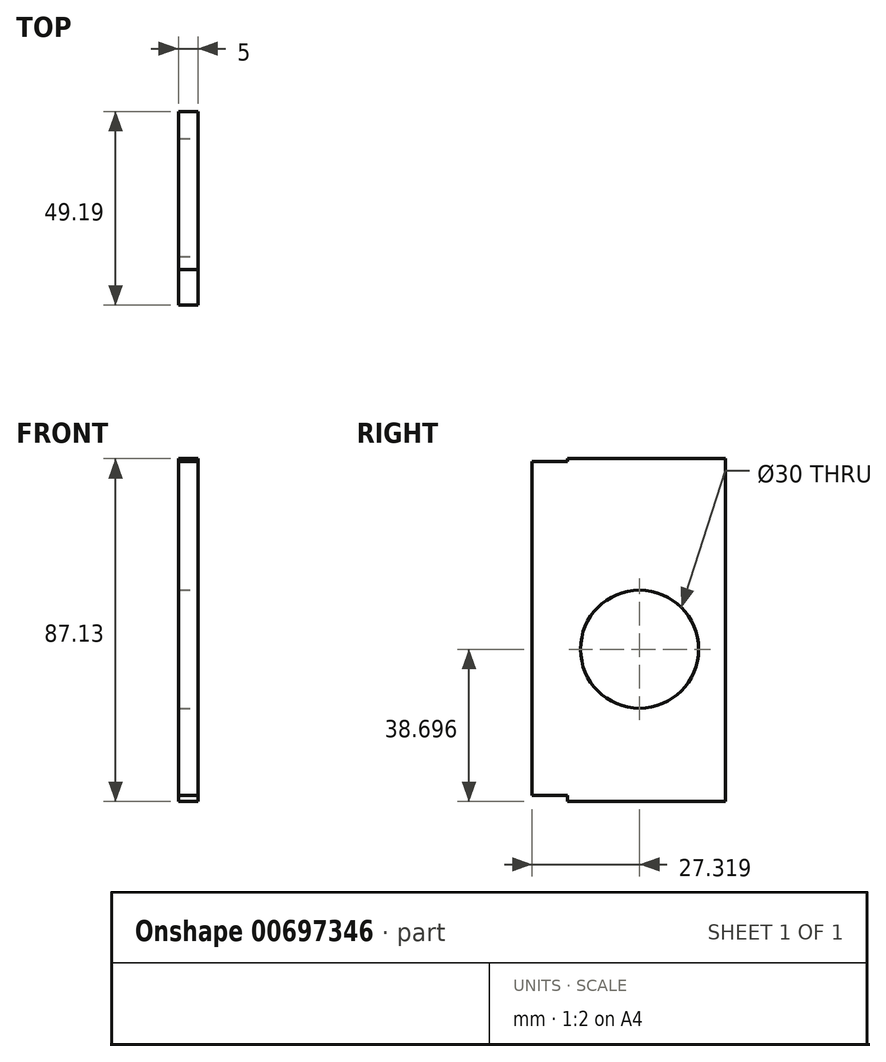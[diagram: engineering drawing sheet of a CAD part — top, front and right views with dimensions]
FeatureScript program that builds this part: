
annotation { "Feature Type Name" : "Feature", "Feature Type Description" : "" }
export const myFeature = defineFeature(function(context is Context, id is Id, definition is map)
    precondition{}
    {
        {
            var Q0;
            Q0=qCreatedBy(makeId("Right.planeOp"),FACE);
            var sketch = newSketch(context, id + "F0", { "sketchPlane" : qUnion([Q0])});
            skLineSegment(sketch, "E0.bottom", {"start": v(0, 24.3) * mm, "end": v(-40.2, 24.3) * mm});
            skLineSegment(sketch, "E0.top", {"start": v(0, -62.83) * mm, "end": v(-40.2, -62.83) * mm});
            skLineSegment(sketch, "E0.left", {"start": v(0, 24.3) * mm, "end": v(0, -62.83) * mm});
            skLineSegment(sketch, "E0.right", {"start": v(-40.2, 24.3) * mm, "end": v(-40.2, -62.83) * mm});
            skSolve(sketch);
        }
        {
            var Q0;
            Q0 = qSketchRegion(id + "F0", true);
            extrude(context, id + "F1", {"entities" : qUnion([Q0]), "depth" : 5 * mm, "offsetDistance" : 25 * mm});
        }
        {
            var Q0;
            Q0=makeQuery(id+"F1.opExtrude","CAP_FACE",FACE,{"disambiguationData":[OSD([sQuery(id+"F0.wireOp",EDGE,"E0.bottom"),sQuery(id+"F0.wireOp",EDGE,"E0.top"),sQuery(id+"F0.wireOp",EDGE,"E0.left"),sQuery(id+"F0.wireOp",EDGE,"E0.right")])],"isStart":false});
            var sketch = newSketch(context, id + "F2", { "sketchPlane" : qUnion([Q0])});
            skCircle(sketch, "E1", {"center": v(-21.87, -24.13) * mm, "radius": 12.8 * mm});
            skSolve(sketch);
        }
        {
            var Q0;
            Q0=sQuery(id+"F2.wireOp",VERTEX,"E1.center");
            var Q1;
            Q1=makeQuery(id+"F1.opExtrude","SWEPT_BODY",BODY,{"disambiguationData":[OSD([sQuery(id+"F0.wireOp",EDGE,"E0.bottom"),sQuery(id+"F0.wireOp",EDGE,"E0.top"),sQuery(id+"F0.wireOp",EDGE,"E0.left"),sQuery(id+"F0.wireOp",EDGE,"E0.right")])]});
            hole(context, id + "F3", {"style" : HoleStyle.SIMPLE, "endStyle" : HoleEndStyle.THROUGH, "holeDiameter" : 30 * mm, "majorDiameter" : 5 * mm, "isTappedThrough" : true, "tappedDepth" : 12 * mm, "tapClearance" : 3, "locations" : qUnion([Q0]), "scope" : qUnion([Q1])});
        }
        {
            var Q0;
            Q0=qCreatedBy(makeId("Right.planeOp"),FACE);
            var sketch = newSketch(context, id + "F4", { "sketchPlane" : qUnion([Q0])});
            skLineSegment(sketch, "E2.bottom", {"start": v(-39.07, 23.6) * mm, "end": v(-49.19, 23.6) * mm});
            skLineSegment(sketch, "E2.top", {"start": v(-39.07, -61.25) * mm, "end": v(-49.19, -61.25) * mm});
            skLineSegment(sketch, "E2.left", {"start": v(-39.07, 23.6) * mm, "end": v(-39.07, -61.25) * mm});
            skLineSegment(sketch, "E2.right", {"start": v(-49.19, 23.6) * mm, "end": v(-49.19, -61.25) * mm});
            skSolve(sketch);
        }
        {
            var Q0;
            Q0 = qSketchRegion(id + "F4", true);
            extrude(context, id + "F5", {"entities" : qUnion([Q0]), "operationType" : NewBodyOperationType.ADD, "depth" : 5 * mm, "offsetDistance" : 25 * mm});
        }
    });
